# Revit family: MixerTap_Wall_Abey_PocoP_BathShower_Circular_FaceBased
name_source: partatom
category: Plumbing Fixtures
units: mm (PartAtom-declared; Revit-internal decimal feet)

## family parameters
Cut with Voids When Loaded = No
Host = Face
Maintain Annotation Orientation = No
OmniClass Number = 23.31.11.19
OmniClass Title = Faucet Mixing Valves
Part Type = Normal
Room Calculation Point = No
Round Connector Dimension = Use Diameter
Shared = No

## types (3) — shared parameters
Assembly Code = C1030210
CW Connection = Yes
Default Elevation = 0 mm
Description = Poco P Wall Diverter Mixer
HW Connection = Yes
IfcExportAs = ifcValve
IfcExportType = FAUCET
Manufacturer = Abey
ManufacturerOverallDepth = 60 mm
ManufacturerOverallHeight = 150 mm
ManufacturerOverallWidth = 65 mm
ManufacturerURLProductSpecific = https://www.abeyspecifier.com.au
ModifiedIssue = 20251103 $
URL = https://www.abey.com.au
Uniclass2015Code = Pr_40_20_87_55
Uniclass2015Title = Mixer taps
Uniclass2015Version = Products v1.38
Vent Connection = No
Waste Connection = No
zero-valued in all types: Cost

## per-type parameters (varying)
| type | BodyMaterial | KnurledMaterial | ManufacturerSpecCode | Model | Type Comments |
| Gun Metal (8SHD-EXT-GM-LF) | Metal_Abey_GunMetal | Metal_Abey_GunMetal_Knurled | 8SHD-EXT-GM-LF | 8SHD-EXT-GM-LF | Mixer Tap - Wall - Gun Metal |
| Brushed Nickel (8SHD-EXT-BN-LF) | Metal_Abey_BrushedNickel | Metal_Abey_BrushedNickel_Knurled | 8SHD-EXT-BN-LF | 8SHD-EXT-BN-LF | Mixer Tap - Wall - Brushed Nickel |
| Brushed Brass (8SHD-EXT-BB-LF) | Metal_Abey_Brass | Metal_Abey_Brass_Knurled | 8SHD-EXT-BB-LF | 8SHD-EXT-BB-LF | Mixer Tap - Wall - Brushed Brass |

## geometry (parser evidence)
native form markers: Sweep x5
no freeform markers — native parametric forms only
